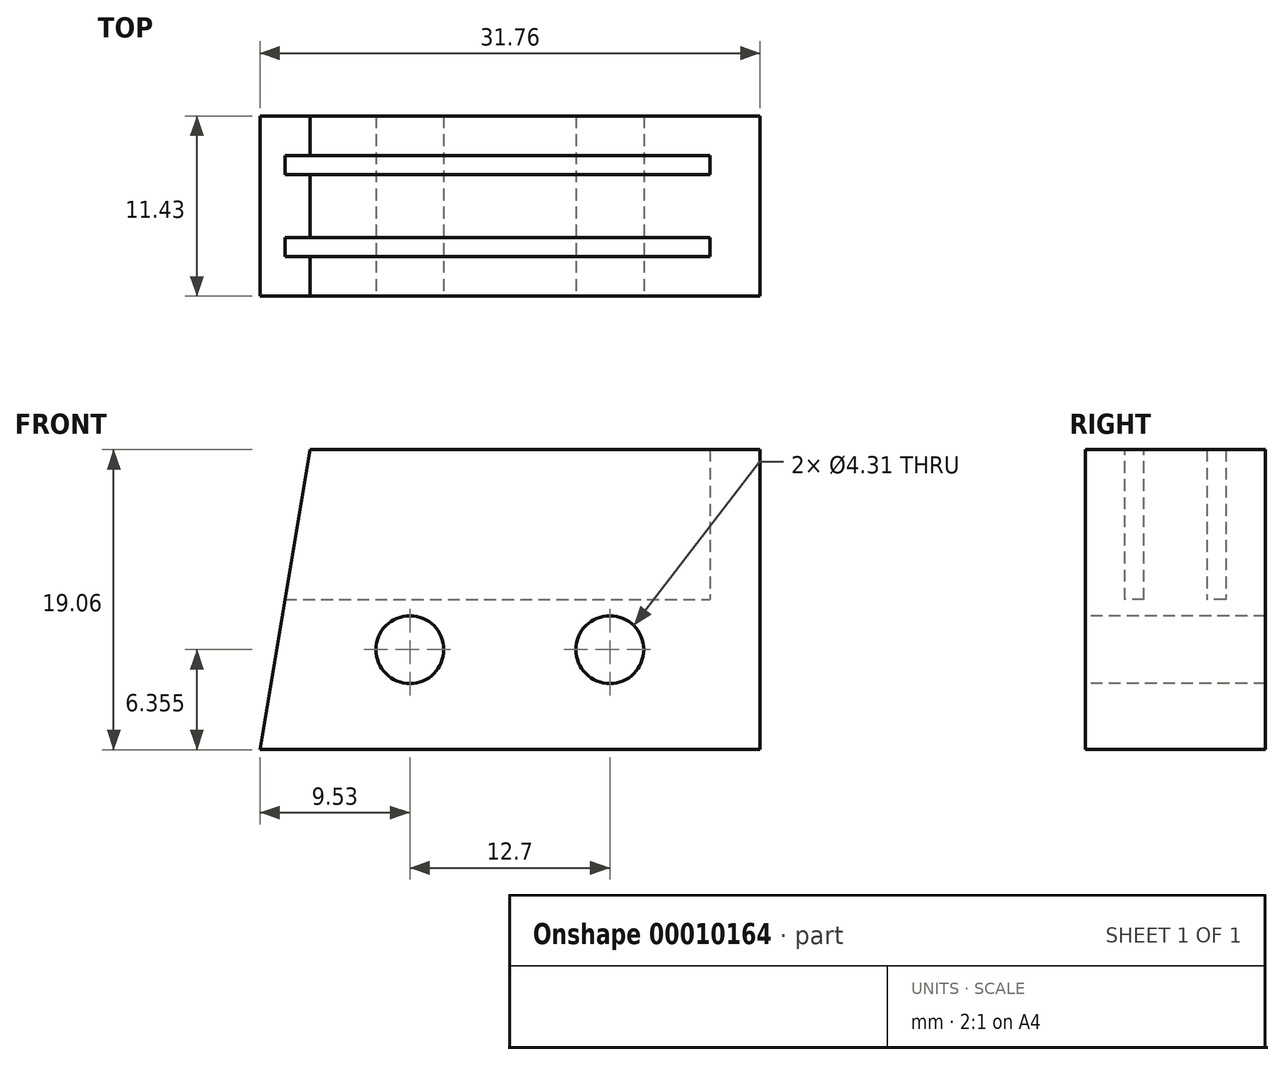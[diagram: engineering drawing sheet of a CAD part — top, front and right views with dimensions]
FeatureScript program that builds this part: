
annotation { "Feature Type Name" : "Feature", "Feature Type Description" : "" }
export const myFeature = defineFeature(function(context is Context, id is Id, definition is map)
    precondition{}
    {
        {
            var Q0;
            Q0=qCreatedBy(makeId("Top.planeOp"),FACE);
            var sketch = newSketch(context, id + "F0", { "sketchPlane" : qUnion([Q0])});
            skLineSegment(sketch, "E0.rect.bottom", {"start": v(15.88, 9.52) * mm, "end": v(-15.88, 9.52) * mm});
            skLineSegment(sketch, "E0.rect.top", {"start": v(15.88, -9.53) * mm, "end": v(-15.88, -9.53) * mm});
            skLineSegment(sketch, "E0.rect.left", {"start": v(15.88, 9.52) * mm, "end": v(15.88, -9.53) * mm});
            skLineSegment(sketch, "E0.rect.right", {"start": v(-15.88, 9.52) * mm, "end": v(-15.88, -9.53) * mm});
            skPoint(sketch, "E0.rect.middle", {"position": v(0, 0) * mm});
            skSolve(sketch);
        }
        {
            var Q0;
            Q0=qSketchRegion(id+"F0",true);
            extrude(context, id + "F1", {"entities" : qUnion([Q0]), "depth" : 11.43 * mm});
        }
        {
            var Q0;
            Q0=makeQuery(id+"F1.opExtrude","CAP_FACE",FACE,{"disambiguationData":[OSD([sQuery(id+"F0.wireOp",EDGE,"E0.rect.bottom"),sQuery(id+"F0.wireOp",EDGE,"E0.rect.top"),sQuery(id+"F0.wireOp",EDGE,"E0.rect.left"),sQuery(id+"F0.wireOp",EDGE,"E0.rect.right")])],"isStart":false});
            var sketch = newSketch(context, id + "F2", { "sketchPlane" : qUnion([Q0])});
            skCircle(sketch, "E1", {"center": v(-6.35, -3.18) * mm, "radius": 2.15 * mm});
            skCircle(sketch, "E2", {"center": v(6.35, -3.18) * mm, "radius": 2.15 * mm});
            skSolve(sketch);
        }
        {
            var Q0;
            Q0=qSketchRegion(id+"F2",true);
            extrude(context, id + "F3", {"entities" : qUnion([Q0]), "operationType" : NewBodyOperationType.REMOVE, "endBound" : BoundingType.UP_TO_NEXT, "oppositeDirection" : true, "depth" : 25.4 * mm});
        }
        {
            var Q0;
            Q0=makeQuery(id+"F1.opExtrude","SWEPT_FACE",FACE,{"disambiguationData":[OSD([sQuery(id+"F0.wireOp",EDGE,"E0.rect.bottom")])]});
            var sketch = newSketch(context, id + "F4", { "sketchPlane" : qUnion([Q0])});
            skLineSegment(sketch, "E3.rect.bottom", {"start": v(19.05, 2.51) * mm, "end": v(-19.05, 2.51) * mm});
            skLineSegment(sketch, "E3.rect.top", {"start": v(19.05, 3.71) * mm, "end": v(-19.05, 3.71) * mm});
            skLineSegment(sketch, "E3.rect.left", {"start": v(19.05, 2.51) * mm, "end": v(19.05, 3.71) * mm});
            skLineSegment(sketch, "E3.rect.right", {"start": v(-19.05, 2.51) * mm, "end": v(-19.05, 3.71) * mm});
            skPoint(sketch, "E3.rect.middle", {"position": v(0, 3.11) * mm});
            skLineSegment(sketch, "E4", {"start": v(-15.88, 5.71) * mm, "end": v(15.88, 5.72) * mm, "construction": true});
            skLineSegment(sketch, "E5.rect.bottom", {"start": v(-15.88, 7.71) * mm, "end": v(15.88, 7.71) * mm});
            skLineSegment(sketch, "E5.rect.top", {"start": v(-15.88, 8.91) * mm, "end": v(15.88, 8.91) * mm});
            skLineSegment(sketch, "E5.rect.left", {"start": v(-15.88, 7.71) * mm, "end": v(-15.88, 8.91) * mm});
            skLineSegment(sketch, "E5.rect.right", {"start": v(15.88, 7.71) * mm, "end": v(15.88, 8.91) * mm});
            skPoint(sketch, "E5.rect.middle", {"position": v(0, 8.31) * mm});
            skSolve(sketch);
        }
        {
            var Q0;
            Q0=qSketchRegion(id+"F4",true);
            extrude(context, id + "F5", {"entities" : qUnion([Q0]), "operationType" : NewBodyOperationType.REMOVE, "oppositeDirection" : true, "depth" : 9.52 * mm});
        }
        {
            var Q0;
            Q0=qCreatedBy(makeId("Front.planeOp"),FACE);
            var sketch = newSketch(context, id + "F6", { "sketchPlane" : qUnion([Q0])});
            skLineSegment(sketch, "E6", {"start": v(77.64, 0) * mm, "end": v(-79.2, 0) * mm, "construction": true});
            skSolve(sketch);
        }
        {
            var Q0;
            Q0=makeQuery(id+"F1.opExtrude","CAP_FACE",FACE,{"disambiguationData":[OSD([sQuery(id+"F0.wireOp",EDGE,"E0.rect.bottom"),sQuery(id+"F0.wireOp",EDGE,"E0.rect.top"),sQuery(id+"F0.wireOp",EDGE,"E0.rect.left"),sQuery(id+"F0.wireOp",EDGE,"E0.rect.right")])],"isStart":false});
            var sketch = newSketch(context, id + "F7", { "sketchPlane" : qUnion([Q0])});
            skLineSegment(sketch, "E7", {"start": v(-15.88, -9.53) * mm, "end": v(-15.88, 9.52) * mm});
            skLineSegment(sketch, "E8", {"start": v(-15.88, 9.52) * mm, "end": v(-12.7, 9.52) * mm});
            skLineSegment(sketch, "E9", {"start": v(-12.7, 9.53) * mm, "end": v(-15.88, -9.53) * mm});
            skSolve(sketch);
        }
        {
            var Q0;
            Q0=qSketchRegion(id+"F7",true);
            var Q1;
            Q1=makeQuery(id+"F1.opExtrude","CAP_FACE",FACE,{"disambiguationData":[OSD([sQuery(id+"F0.wireOp",EDGE,"E0.rect.bottom"),sQuery(id+"F0.wireOp",EDGE,"E0.rect.top"),sQuery(id+"F0.wireOp",EDGE,"E0.rect.left"),sQuery(id+"F0.wireOp",EDGE,"E0.rect.right")])],"isStart":true});
            extrude(context, id + "F8", {"entities" : qUnion([Q0]), "operationType" : NewBodyOperationType.REMOVE, "endBound" : BoundingType.UP_TO_SURFACE, "oppositeDirection" : true, "endBoundEntityFace" : qUnion([Q1]), "depth" : 25.4 * mm});
        }
        {
            var Q0;
            Q0=makeQuery(id+"F1.opExtrude","SWEPT_BODY",BODY,{"disambiguationData":[OSD([sQuery(id+"F0.wireOp",EDGE,"E0.rect.bottom"),sQuery(id+"F0.wireOp",EDGE,"E0.rect.top"),sQuery(id+"F0.wireOp",EDGE,"E0.rect.left"),sQuery(id+"F0.wireOp",EDGE,"E0.rect.right")])]});
            var Q1;
            Q1=sQuery(id+"F6.wireOp",EDGE,"E6");
            transform(context, id + "F9", {"entities" : qUnion([Q0]), "transformType" : TransformType.ROTATION, "transformAxis" : qUnion([Q1]), "angle" : 90 * degree, "oppositeDirection" : true, "makeCopy" : false});
        }
        {
            var Q0;
            Q0=makeQuery(id+"F1.opExtrude","CAP_FACE",FACE,{"disambiguationData":[OSD([sQuery(id+"F0.wireOp",EDGE,"E0.rect.bottom"),sQuery(id+"F0.wireOp",EDGE,"E0.rect.top"),sQuery(id+"F0.wireOp",EDGE,"E0.rect.left"),sQuery(id+"F0.wireOp",EDGE,"E0.rect.right")])],"isStart":false});
            var sketch = newSketch(context, id + "F10", { "sketchPlane" : qUnion([Q0])});
            skLineSegment(sketch, "E10.bottom", {"start": v(15.88, 9.52) * mm, "end": v(12.7, 9.52) * mm});
            skLineSegment(sketch, "E10.top", {"start": v(15.88, -9.53) * mm, "end": v(12.7, -9.53) * mm});
            skLineSegment(sketch, "E10.left", {"start": v(15.88, 9.52) * mm, "end": v(15.88, -9.53) * mm});
            skLineSegment(sketch, "E10.right", {"start": v(12.7, 9.53) * mm, "end": v(12.7, -9.53) * mm});
            skSolve(sketch);
        }
        {
            var Q0;
            Q0=qSketchRegion(id+"F10",true);
            var Q1;
            Q1=makeQuery(id+"F1.opExtrude","CAP_FACE",FACE,{"disambiguationData":[OSD([sQuery(id+"F0.wireOp",EDGE,"E0.rect.bottom"),sQuery(id+"F0.wireOp",EDGE,"E0.rect.top"),sQuery(id+"F0.wireOp",EDGE,"E0.rect.left"),sQuery(id+"F0.wireOp",EDGE,"E0.rect.right")])],"isStart":true});
            extrude(context, id + "F11", {"entities" : qUnion([Q0]), "operationType" : NewBodyOperationType.ADD, "endBound" : BoundingType.UP_TO_SURFACE, "oppositeDirection" : true, "endBoundEntityFace" : qUnion([Q1]), "depth" : 25.4 * mm});
        }
    });
